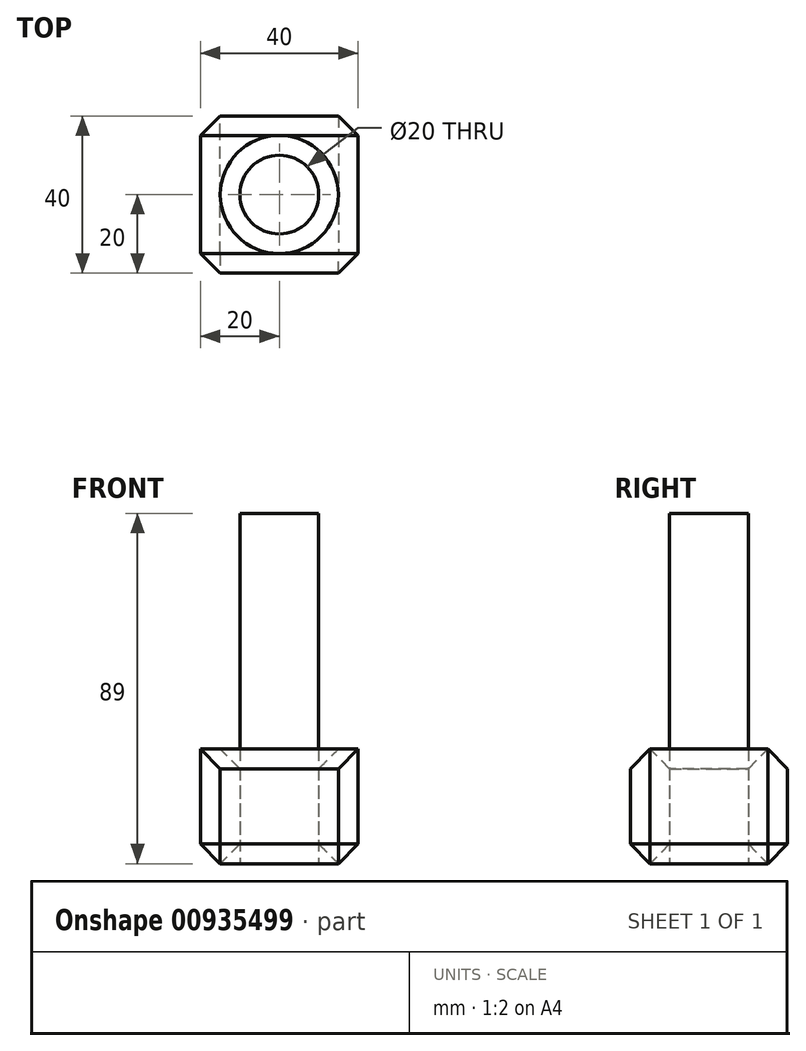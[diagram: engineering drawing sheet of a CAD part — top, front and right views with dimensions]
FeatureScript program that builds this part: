
annotation { "Feature Type Name" : "Feature", "Feature Type Description" : "" }
export const myFeature = defineFeature(function(context is Context, id is Id, definition is map)
    precondition{}
    {
        {
            var Q0;
            Q0=qCreatedBy(makeId("Top.planeOp"),FACE);
            var sketch = newSketch(context, id + "F0", { "sketchPlane" : qUnion([Q0])});
            skLineSegment(sketch, "E0.bottom", {"start": v(20, -20) * mm, "end": v(-20, -20) * mm});
            skLineSegment(sketch, "E0.top", {"start": v(20, 20) * mm, "end": v(-20, 20) * mm});
            skLineSegment(sketch, "E0.left", {"start": v(20, -20) * mm, "end": v(20, 20) * mm});
            skLineSegment(sketch, "E0.right", {"start": v(-20, -20) * mm, "end": v(-20, 20) * mm});
            skPoint(sketch, "E0.middle", {"position": v(0, 0) * mm});
            skPoint(sketch, "E1.middle", {"position": v(-20, 0) * mm});
            skCircle(sketch, "E2", {"center": v(0, 0) * mm, "radius": 10 * mm});
            skSolve(sketch);
        }
        {
            var Q0;
            Q0=makeQuery(id+"F0.imprint","IMPRINT",FACE,{"disambiguationData":[TD([[makeQuery(id+"F0.imprint","IMPRINT",EDGE,{"derivedFrom":sQuery(id+"F0.wireOp",EDGE,"E0.bottom")}),-1.0]])]});
            extrude(context, id + "F1", {"entities" : qUnion([Q0]), "depth" : 29.1 * mm, "offsetDistance" : 25 * mm});
        }
        {
            var Q0;
            Q0=makeQuery(id+"F0.imprint","IMPRINT",FACE,{"disambiguationData":[TD([[makeQuery(id+"F0.imprint","IMPRINT",EDGE,{"derivedFrom":sQuery(id+"F0.wireOp",EDGE,"E2")}),1.0]])]});
            extrude(context, id + "F2", {"entities" : qUnion([Q0]), "depth" : 89 * mm, "offsetDistance" : 25 * mm});
        }
        {
            var Q0;
            Q0=makeQuery(id+"F1.opExtrude","CAP_EDGE",EDGE,{"disambiguationData":[OSD([sQuery(id+"F0.wireOp",EDGE,"E0.bottom")])],"isStart":false});
            var Q1;
            Q1=makeQuery(id+"F1.opExtrude","CAP_EDGE",EDGE,{"disambiguationData":[OSD([sQuery(id+"F0.wireOp",EDGE,"E0.bottom")])],"isStart":true});
            var Q2;
            Q2=makeQuery(id+"F1.opExtrude","SWEPT_FACE",FACE,{"disambiguationData":[OSD([sQuery(id+"F0.wireOp",EDGE,"E0.bottom")])]});
            var Q3;
            Q3=makeQuery(id+"F1.opExtrude","SWEPT_FACE",FACE,{"disambiguationData":[OSD([sQuery(id+"F0.wireOp",EDGE,"E0.top")])]});
            var Q4;
            Q4=makeQuery(id+"F1.opExtrude","CAP_EDGE",EDGE,{"disambiguationData":[OSD([sQuery(id+"F0.wireOp",EDGE,"E0.top")])],"isStart":true});
            var Q5;
            Q5=makeQuery(id+"F1.opExtrude","CAP_EDGE",EDGE,{"disambiguationData":[OSD([sQuery(id+"F0.wireOp",EDGE,"E0.top")])],"isStart":false});
            var Q6;
            Q6=makeQuery(id+"F1.opExtrude","CAP_EDGE",EDGE,{"disambiguationData":[OSD([sQuery(id+"F0.wireOp",EDGE,"E2")])],"isStart":false});
            var Q7;
            Q7=makeQuery(id+"F1.opExtrude","CAP_FACE",FACE,{"disambiguationData":[OSD([sQuery(id+"F0.wireOp",EDGE,"E0.bottom"),sQuery(id+"F0.wireOp",EDGE,"E0.top"),sQuery(id+"F0.wireOp",EDGE,"E0.left"),sQuery(id+"F0.wireOp",EDGE,"E0.right"),sQuery(id+"F0.wireOp",EDGE,"E2")])],"isStart":true});
            var Q8;
            Q8=makeQuery(id+"F1.opExtrude","CAP_EDGE",EDGE,{"disambiguationData":[OSD([sQuery(id+"F0.wireOp",EDGE,"E2")])],"isStart":true});
            chamfer(context, id + "F3", {"entities" : qUnion([Q0, Q1, Q2, Q3, Q4, Q5, Q6, Q7, Q8]), "width" : 5 * mm, "tangentPropagation" : true});
        }
    });
